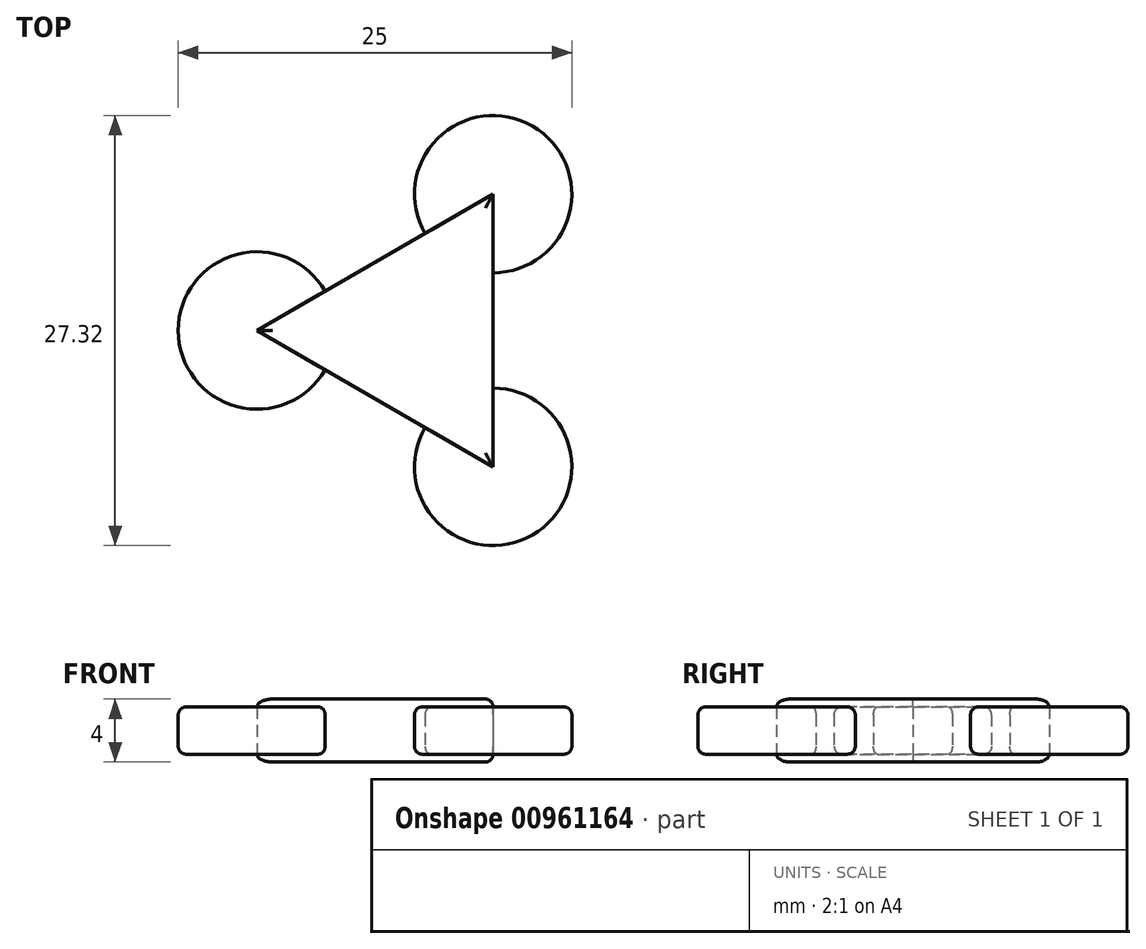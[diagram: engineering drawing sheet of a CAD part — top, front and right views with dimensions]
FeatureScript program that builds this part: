
annotation { "Feature Type Name" : "Feature", "Feature Type Description" : "" }
export const myFeature = defineFeature(function(context is Context, id is Id, definition is map)
    precondition{}
    {
        {
            var Q0;
            Q0=qCreatedBy(makeId("Top.planeOp"),FACE);
            var sketch = newSketch(context, id + "F0", { "sketchPlane" : qUnion([Q0])});
            skCircle(sketch, "E0", {"center": v(0, 0) * mm, "radius": 5 * mm});
            skCircle(sketch, "E1.cCircle", {"center": v(0, 0) * mm, "radius": 5 * mm, "construction": true});
            skLineSegment(sketch, "E1.0", {"start": v(5, 8.66) * mm, "end": v(5, -8.66) * mm});
            skLineSegment(sketch, "E1.1", {"start": v(5, -8.66) * mm, "end": v(-10, 0) * mm});
            skLineSegment(sketch, "E1.2", {"start": v(-10, 0) * mm, "end": v(5, 8.66) * mm});
            skPoint(sketch, "E1.0.midPoint", {"position": v(5, 0) * mm});
            skCircle(sketch, "E2", {"center": v(5, 8.66) * mm, "radius": 5 * mm});
            skCircle(sketch, "E3", {"center": v(5, -8.66) * mm, "radius": 5 * mm});
            skCircle(sketch, "E4", {"center": v(-10, 0) * mm, "radius": 5 * mm});
            skSolve(sketch);
        }
        {
            var Q0;
            {var subQ0=sQuery(id+"F0.wireOp",EDGE,"E1.2");var subQ1=sQuery(id+"F0.wireOp",EDGE,"E1.1");var subQ2=makeQuery(id+"F0.imprint","INTERSECT",VERTEX,{"derivedFrom":[subQ1,subQ0]});Q0=makeQuery(id+"F0.imprint","IMPRINT",FACE,{"disambiguationData":[TD([[makeQuery(id+"F0.imprint","IMPRINT",EDGE,{"disambiguationData":[TD([[subQ2,1.0]])],"derivedFrom":subQ1}),-1.0]])]});}
            var Q1;
            {var subQ0=sQuery(id+"F0.wireOp",EDGE,"E1.2");var subQ1=sQuery(id+"F0.wireOp",EDGE,"E0");var subQ2=makeQuery(id+"F0.imprint","INTERSECT",VERTEX,{"derivedFrom":[subQ1,subQ0]});Q1=makeQuery(id+"F0.imprint","IMPRINT",FACE,{"disambiguationData":[TD([[makeQuery(id+"F0.imprint","IMPRINT",EDGE,{"disambiguationData":[TD([[subQ2,1.0]])],"derivedFrom":subQ1}),-1.0]])]});}
            var Q2;
            {var subQ0=sQuery(id+"F0.wireOp",EDGE,"E1.1");var subQ1=sQuery(id+"F0.wireOp",EDGE,"E1.0");var subQ2=makeQuery(id+"F0.imprint","INTERSECT",VERTEX,{"derivedFrom":[subQ1,subQ0]});Q2=makeQuery(id+"F0.imprint","IMPRINT",FACE,{"disambiguationData":[TD([[makeQuery(id+"F0.imprint","IMPRINT",EDGE,{"disambiguationData":[TD([[subQ2,1.0]])],"derivedFrom":subQ1}),-1.0]])]});}
            var Q3;
            {var subQ0=sQuery(id+"F0.wireOp",EDGE,"E1.0");var subQ1=sQuery(id+"F0.wireOp",EDGE,"E0");var subQ2=makeQuery(id+"F0.imprint","INTERSECT",VERTEX,{"derivedFrom":[subQ1,subQ0]});Q3=makeQuery(id+"F0.imprint","IMPRINT",FACE,{"disambiguationData":[TD([[makeQuery(id+"F0.imprint","IMPRINT",EDGE,{"disambiguationData":[TD([[subQ2,1.0]])],"derivedFrom":subQ1}),-1.0]])]});}
            var Q4;
            {var subQ0=sQuery(id+"F0.wireOp",EDGE,"E1.2");var subQ1=sQuery(id+"F0.wireOp",EDGE,"E0");var subQ2=makeQuery(id+"F0.imprint","INTERSECT",VERTEX,{"derivedFrom":[subQ1,subQ0]});Q4=makeQuery(id+"F0.imprint","IMPRINT",FACE,{"disambiguationData":[TD([[makeQuery(id+"F0.imprint","IMPRINT",EDGE,{"disambiguationData":[TD([[subQ2,-1.0]])],"derivedFrom":subQ1}),-1.0]])]});}
            var Q5;
            {var subQ0=sQuery(id+"F0.wireOp",EDGE,"E1.1");var subQ1=sQuery(id+"F0.wireOp",EDGE,"E0");var subQ2=makeQuery(id+"F0.imprint","INTERSECT",VERTEX,{"derivedFrom":[subQ1,subQ0]});Q5=makeQuery(id+"F0.imprint","IMPRINT",FACE,{"disambiguationData":[TD([[makeQuery(id+"F0.imprint","IMPRINT",EDGE,{"disambiguationData":[TD([[subQ2,1.0]])],"derivedFrom":subQ1}),-1.0]])]});}
            var Q6;
            {var subQ0=sQuery(id+"F0.wireOp",EDGE,"E1.0");var subQ1=sQuery(id+"F0.wireOp",EDGE,"E0");var subQ2=makeQuery(id+"F0.imprint","INTERSECT",VERTEX,{"derivedFrom":[subQ1,subQ0]});Q6=makeQuery(id+"F0.imprint","IMPRINT",FACE,{"disambiguationData":[TD([[makeQuery(id+"F0.imprint","IMPRINT",EDGE,{"disambiguationData":[TD([[subQ2,-1.0]])],"derivedFrom":subQ1}),-1.0]])]});}
            var Q7;
            {var subQ0=sQuery(id+"F0.wireOp",EDGE,"E0");var subQ5=makeQuery(id+"F0.imprint","INTERSECT",VERTEX,{"derivedFrom":[subQ0,sQuery(id+"F0.wireOp",EDGE,"E1.0")]});Q7=makeQuery(id+"F0.imprint","IMPRINT",FACE,{"disambiguationData":[TD([[makeQuery(id+"F0.imprint","IMPRINT",EDGE,{"disambiguationData":[TD([[subQ5,-1.0]])],"derivedFrom":subQ0}),1.0]])]});}
            var Q8;
            {var subQ0=sQuery(id+"F0.wireOp",EDGE,"E1.2");var subQ1=sQuery(id+"F0.wireOp",EDGE,"E1.0");var subQ2=makeQuery(id+"F0.imprint","INTERSECT",VERTEX,{"derivedFrom":[subQ1,subQ0]});Q8=makeQuery(id+"F0.imprint","IMPRINT",FACE,{"disambiguationData":[TD([[makeQuery(id+"F0.imprint","IMPRINT",EDGE,{"disambiguationData":[TD([[subQ2,-1.0]])],"derivedFrom":subQ1}),-1.0]])]});}
            var Q9;
            {var subQ0=sQuery(id+"F0.wireOp",EDGE,"E1.1");var subQ1=sQuery(id+"F0.wireOp",EDGE,"E0");var subQ2=makeQuery(id+"F0.imprint","INTERSECT",VERTEX,{"derivedFrom":[subQ1,subQ0]});Q9=makeQuery(id+"F0.imprint","IMPRINT",FACE,{"disambiguationData":[TD([[makeQuery(id+"F0.imprint","IMPRINT",EDGE,{"disambiguationData":[TD([[subQ2,-1.0]])],"derivedFrom":subQ1}),-1.0]])]});}
            extrude(context, id + "F1", {"entities" : qUnion([Q0, Q1, Q2, Q3, Q4, Q5, Q6, Q7, Q8, Q9]), "surfaceOperationType" : NewSurfaceOperationType.ADD, "depth" : 2 * mm, "offsetDistance" : 25.4 * mm, "hasSecondDirection" : true, "secondDirectionOppositeDirection" : true, "secondDirectionDepth" : 2 * mm});
        }
        {
            var Q0;
            {var subQ0=sQuery(id+"F0.wireOp",EDGE,"E1.1");var subQ1=sQuery(id+"F0.wireOp",EDGE,"E1.0");var subQ2=makeQuery(id+"F0.imprint","INTERSECT",VERTEX,{"derivedFrom":[subQ1,subQ0]});Q0=makeQuery(id+"F0.imprint","IMPRINT",FACE,{"disambiguationData":[TD([[makeQuery(id+"F0.imprint","IMPRINT",EDGE,{"disambiguationData":[TD([[subQ2,1.0]])],"derivedFrom":subQ1}),1.0]])]});}
            var Q1;
            {var subQ0=sQuery(id+"F0.wireOp",EDGE,"E1.2");var subQ1=sQuery(id+"F0.wireOp",EDGE,"E1.1");var subQ2=makeQuery(id+"F0.imprint","INTERSECT",VERTEX,{"derivedFrom":[subQ1,subQ0]});Q1=makeQuery(id+"F0.imprint","IMPRINT",FACE,{"disambiguationData":[TD([[makeQuery(id+"F0.imprint","IMPRINT",EDGE,{"disambiguationData":[TD([[subQ2,1.0]])],"derivedFrom":subQ1}),1.0]])]});}
            var Q2;
            {var subQ0=sQuery(id+"F0.wireOp",EDGE,"E1.2");var subQ1=sQuery(id+"F0.wireOp",EDGE,"E1.0");var subQ2=makeQuery(id+"F0.imprint","INTERSECT",VERTEX,{"derivedFrom":[subQ1,subQ0]});Q2=makeQuery(id+"F0.imprint","IMPRINT",FACE,{"disambiguationData":[TD([[makeQuery(id+"F0.imprint","IMPRINT",EDGE,{"disambiguationData":[TD([[subQ2,-1.0]])],"derivedFrom":subQ1}),1.0]])]});}
            extrude(context, id + "F2", {"entities" : qUnion([Q0, Q1, Q2]), "depth" : 1.5 * mm, "offsetDistance" : 25.4 * mm, "hasSecondDirection" : true, "secondDirectionOppositeDirection" : true, "secondDirectionDepth" : 1.5 * mm});
        }
        {
            var Q0;
            Q0=makeQuery(id+"F1.opExtrude","CAP_EDGE",EDGE,{"disambiguationData":[OSD([sQuery(id+"F0.wireOp",EDGE,"E1.2")])],"isStart":false});
            var Q1;
            Q1=makeQuery(id+"F1.opExtrude","CAP_EDGE",EDGE,{"disambiguationData":[OSD([sQuery(id+"F0.wireOp",EDGE,"E1.1")])],"isStart":false});
            var Q2;
            Q2=makeQuery(id+"F1.opExtrude","CAP_EDGE",EDGE,{"disambiguationData":[OSD([sQuery(id+"F0.wireOp",EDGE,"E1.0")])],"isStart":false});
            var Q3;
            Q3=makeQuery(id+"F1.opExtrude","CAP_EDGE",EDGE,{"disambiguationData":[OSD([sQuery(id+"F0.wireOp",EDGE,"E1.0")])],"isStart":true});
            var Q4;
            Q4=makeQuery(id+"F1.opExtrude","CAP_EDGE",EDGE,{"disambiguationData":[OSD([sQuery(id+"F0.wireOp",EDGE,"E1.1")])],"isStart":true});
            var Q5;
            Q5=makeQuery(id+"F1.opExtrude","CAP_EDGE",EDGE,{"disambiguationData":[OSD([sQuery(id+"F0.wireOp",EDGE,"E1.2")])],"isStart":true});
            var Q6;
            Q6=makeQuery(id+"F2.opExtrude","CAP_EDGE",EDGE,{"disambiguationData":[OSD([sQuery(id+"F0.wireOp",EDGE,"E2")])],"isStart":false});
            var Q7;
            Q7=makeQuery(id+"F2.opExtrude","CAP_EDGE",EDGE,{"disambiguationData":[OSD([sQuery(id+"F0.wireOp",EDGE,"E2")])],"isStart":true});
            var Q8;
            Q8=makeQuery(id+"F2.opExtrude","CAP_EDGE",EDGE,{"disambiguationData":[OSD([sQuery(id+"F0.wireOp",EDGE,"E3")])],"isStart":false});
            var Q9;
            Q9=makeQuery(id+"F2.opExtrude","CAP_EDGE",EDGE,{"disambiguationData":[OSD([sQuery(id+"F0.wireOp",EDGE,"E3")])],"isStart":true});
            var Q10;
            Q10=makeQuery(id+"F2.opExtrude","CAP_EDGE",EDGE,{"disambiguationData":[OSD([sQuery(id+"F0.wireOp",EDGE,"E4")])],"isStart":true});
            var Q11;
            Q11=makeQuery(id+"F2.opExtrude","CAP_EDGE",EDGE,{"disambiguationData":[OSD([sQuery(id+"F0.wireOp",EDGE,"E4")])],"isStart":false});
            fillet(context, id + "F3", {"entities" : qUnion([Q0, Q1, Q2, Q3, Q4, Q5, Q6, Q7, Q8, Q9, Q10, Q11]), "radius" : .5 * mm, "tangentPropagation" : true, "allowEdgeOverflow" : false});
        }
    });
